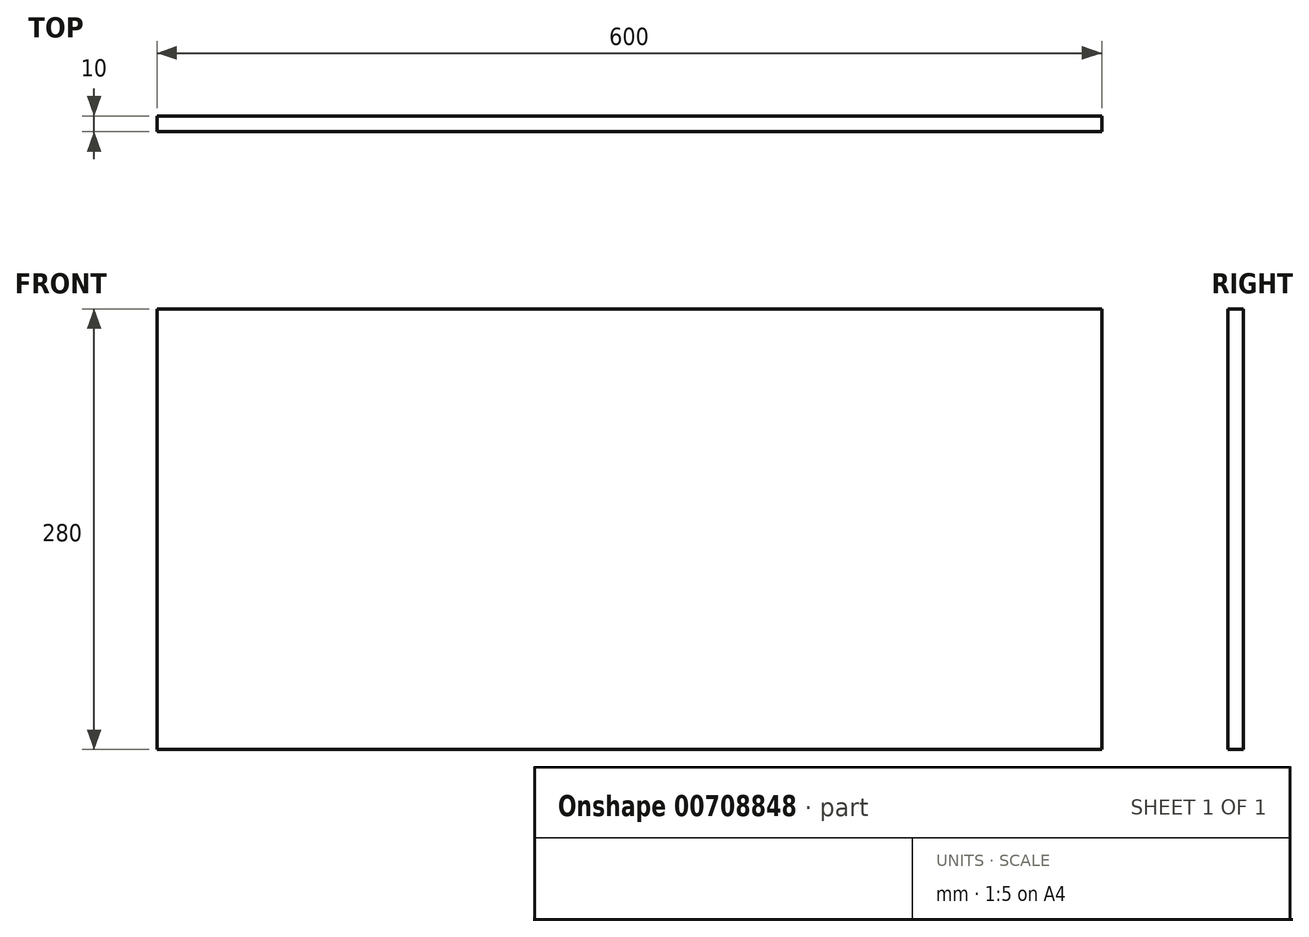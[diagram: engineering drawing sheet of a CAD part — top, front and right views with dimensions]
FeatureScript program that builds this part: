
annotation { "Feature Type Name" : "Feature", "Feature Type Description" : "" }
export const myFeature = defineFeature(function(context is Context, id is Id, definition is map)
    precondition{}
    {
        {
            var Q0;
            Q0=qCreatedBy(makeId("Front.planeOp"),FACE);
            var sketch = newSketch(context, id + "F0", { "sketchPlane" : qUnion([Q0])});
            skLineSegment(sketch, "E0.bottom", {"start": v(0, 0) * mm, "end": v(600, 0) * mm});
            skLineSegment(sketch, "E0.top", {"start": v(0, 280) * mm, "end": v(600, 280) * mm});
            skLineSegment(sketch, "E0.left", {"start": v(0, 0) * mm, "end": v(0, 280) * mm});
            skLineSegment(sketch, "E0.right", {"start": v(600, 0) * mm, "end": v(600, 280) * mm});
            skSolve(sketch);
        }
        {
            var Q0;
            Q0=makeQuery(id+"F0.imprint","IMPRINT",FACE,{"disambiguationData":[TD([[makeQuery(id+"F0.imprint","IMPRINT",EDGE,{"derivedFrom":sQuery(id+"F0.wireOp",EDGE,"E0.bottom")}),1.0]])]});
            extrude(context, id + "F1", {"entities" : qUnion([Q0]), "depth" : 10 * mm, "offsetDistance" : 25 * mm});
        }
    });
